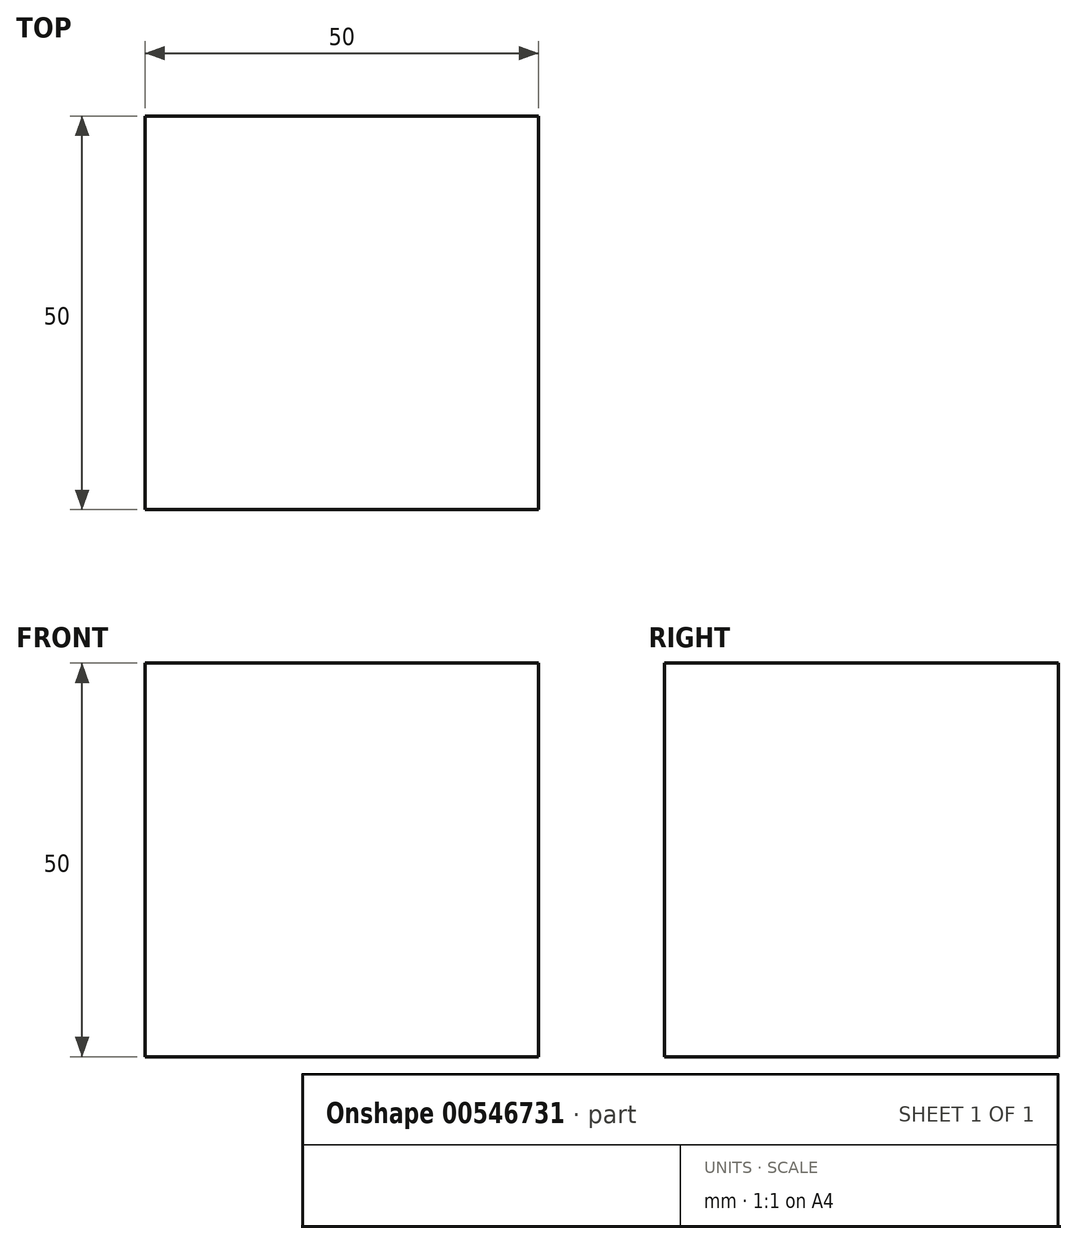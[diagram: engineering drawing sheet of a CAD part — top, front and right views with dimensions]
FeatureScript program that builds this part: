
annotation { "Feature Type Name" : "Feature", "Feature Type Description" : "" }
export const myFeature = defineFeature(function(context is Context, id is Id, definition is map)
    precondition{}
    {
        {
            var Q0;
            Q0=qCreatedBy(makeId("Front.planeOp"),FACE);
            var sketch = newSketch(context, id + "F0", { "sketchPlane" : qUnion([Q0])});
            skLineSegment(sketch, "E0.bottom", {"start": v(0, 0) * mm, "end": v(50, 0) * mm});
            skLineSegment(sketch, "E0.top", {"start": v(0, 50) * mm, "end": v(50, 50) * mm});
            skLineSegment(sketch, "E0.left", {"start": v(0, 0) * mm, "end": v(0, 50) * mm});
            skLineSegment(sketch, "E0.right", {"start": v(50, 0) * mm, "end": v(50, 50) * mm});
            skSolve(sketch);
        }
        {
            var Q0;
            Q0=makeQuery(id+"F0.imprint","IMPRINT",FACE,{"disambiguationData":[TD([[makeQuery(id+"F0.imprint","IMPRINT",EDGE,{"derivedFrom":sQuery(id+"F0.wireOp",EDGE,"E0.bottom")}),1.0]])]});
            extrude(context, id + "F1", {"entities" : qUnion([Q0]), "depth" : 50 * mm, "offsetDistance" : 25 * mm});
        }
    });
